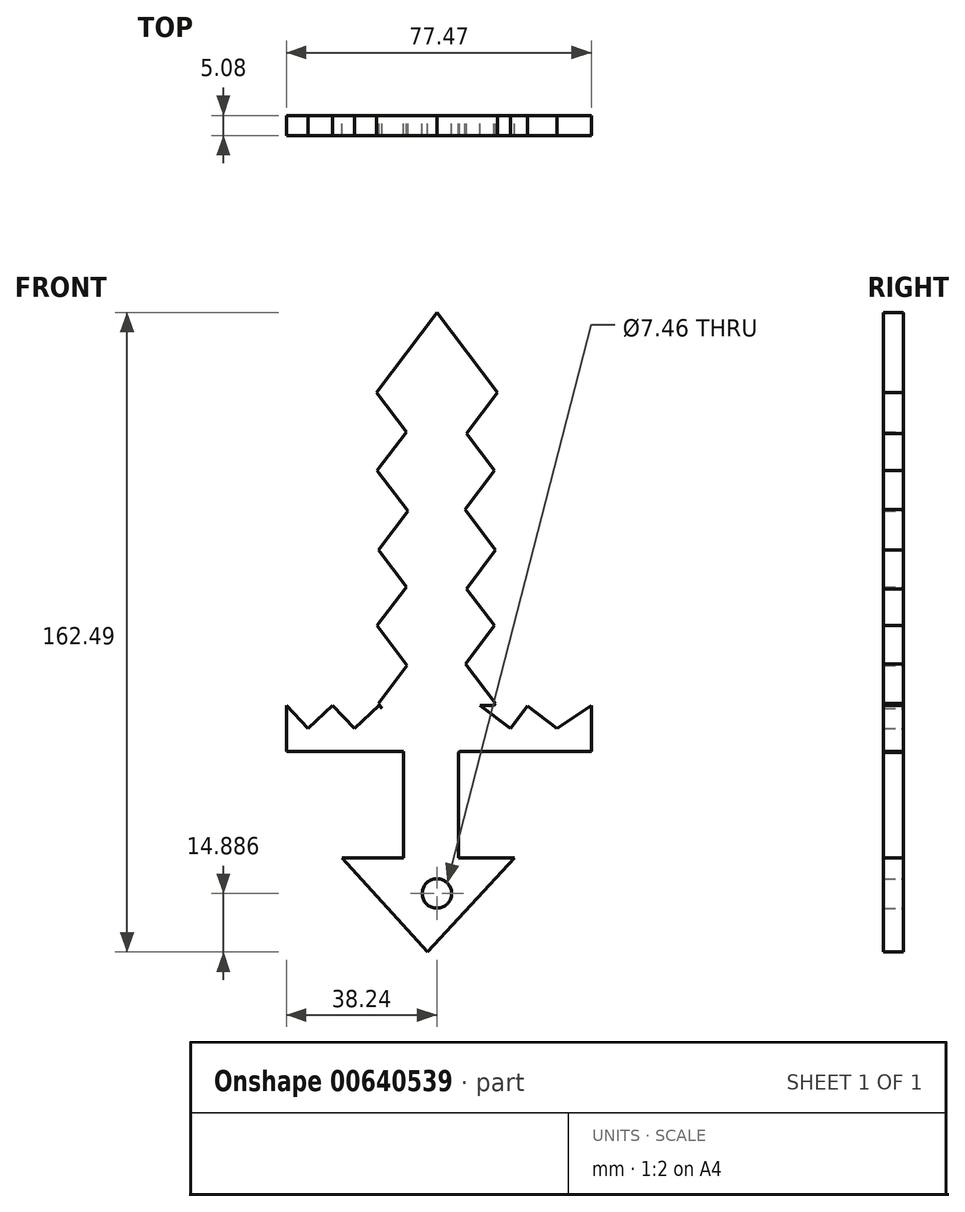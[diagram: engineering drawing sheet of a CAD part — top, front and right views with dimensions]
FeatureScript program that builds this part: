
annotation { "Feature Type Name" : "Feature", "Feature Type Description" : "" }
export const myFeature = defineFeature(function(context is Context, id is Id, definition is map)
    precondition{}
    {
        {
            var Q0;
            Q0=qCreatedBy(makeId("Front.planeOp"),FACE);
            var sketch = newSketch(context, id + "F0", { "sketchPlane" : qUnion([Q0])});
            skLineSegment(sketch, "E0", {"start": v(7.49, 9.92) * mm, "end": v(14.88, 19.71) * mm});
            skLineSegment(sketch, "E1", {"start": v(14.88, 19.71) * mm, "end": v(0, 39.43) * mm});
            skLineSegment(sketch, "E2", {"start": v(0, 39.43) * mm, "end": v(-14.88, 19.71) * mm});
            skLineSegment(sketch, "E3", {"start": v(-14.88, 19.71) * mm, "end": v(-7.79, 10.32) * mm});
            skLineSegment(sketch, "E4", {"start": v(7.26, -9.18) * mm, "end": v(14.58, 0.53) * mm});
            skLineSegment(sketch, "E5", {"start": v(14.58, 0.53) * mm, "end": v(-0.3, 20.24) * mm});
            skLineSegment(sketch, "E6", {"start": v(-0.3, 20.24) * mm, "end": v(-15.17, 0.53) * mm});
            skLineSegment(sketch, "E7", {"start": v(-15.17, 0.53) * mm, "end": v(-7.55, -9.57) * mm});
            skLineSegment(sketch, "E8", {"start": v(7.1, 30.03) * mm, "end": v(14.58, 39.95) * mm});
            skLineSegment(sketch, "E9", {"start": v(14.58, 39.95) * mm, "end": v(-0.3, 59.67) * mm});
            skLineSegment(sketch, "E10", {"start": v(-0.3, 59.67) * mm, "end": v(-15.17, 39.95) * mm});
            skLineSegment(sketch, "E11", {"start": v(-15.17, 39.95) * mm, "end": v(-7.39, 29.64) * mm});
            skLineSegment(sketch, "E12", {"start": v(5.48, -31.73) * mm, "end": v(5.69, -31.45) * mm});
            skLineSegment(sketch, "E13", {"start": v(14.88, -19.27) * mm, "end": v(0, 0.44) * mm});
            skLineSegment(sketch, "E14", {"start": v(0, 0.44) * mm, "end": v(-14.88, -19.27) * mm});
            skLineSegment(sketch, "E15", {"start": v(-14.88, -19.27) * mm, "end": v(-13.97, -20.47) * mm});
            skLineSegment(sketch, "E16", {"start": v(7.49, 49.35) * mm, "end": v(15.35, 59.76) * mm});
            skLineSegment(sketch, "E17", {"start": v(15.35, 59.76) * mm, "end": v(0, 80.1) * mm});
            skLineSegment(sketch, "E18", {"start": v(0, 80.1) * mm, "end": v(-15.35, 59.76) * mm});
            skLineSegment(sketch, "E19", {"start": v(-15.35, 59.76) * mm, "end": v(-7.79, 49.74) * mm});
            skLineSegment(sketch, "E20.bottom", {"start": v(-38.24, -19.7) * mm, "end": v(39.23, -19.7) * mm});
            skLineSegment(sketch, "E20.top", {"start": v(-38.24, -31.45) * mm, "end": v(39.23, -31.45) * mm});
            skLineSegment(sketch, "E20.left", {"start": v(-38.24, -19.7) * mm, "end": v(-38.24, -31.45) * mm});
            skLineSegment(sketch, "E20.right", {"start": v(39.23, -19.7) * mm, "end": v(39.23, -31.45) * mm});
            skLineSegment(sketch, "E21", {"start": v(-8.44, -31.45) * mm, "end": v(-8.44, -58.53) * mm});
            skLineSegment(sketch, "E22", {"start": v(5.48, -31.45) * mm, "end": v(5.48, -58.53) * mm});
            skLineSegment(sketch, "E23", {"start": v(-38.24, -19.7) * mm, "end": v(-32.68, -25.57) * mm});
            skPoint(sketch, "E23.endSnap0", {"position": v(-38.24, -25.57) * mm});
            skLineSegment(sketch, "E24", {"start": v(-32.68, -25.57) * mm, "end": v(-26.48, -19.7) * mm});
            skLineSegment(sketch, "E25", {"start": v(-26.48, -19.7) * mm, "end": v(-20.91, -25.57) * mm});
            skLineSegment(sketch, "E26", {"start": v(-20.91, -25.57) * mm, "end": v(-14.7, -19.7) * mm});
            skLineSegment(sketch, "E27", {"start": v(-14.7, -19.7) * mm, "end": v(-9.14, -25.57) * mm});
            skLineSegment(sketch, "E28", {"start": v(-9.14, -25.57) * mm, "end": v(-1.03, -19.91) * mm});
            skLineSegment(sketch, "E29", {"start": v(-1.03, -19.91) * mm, "end": v(6.47, -25.57) * mm});
            skLineSegment(sketch, "E30", {"start": v(6.47, -25.57) * mm, "end": v(10.9, -19.7) * mm});
            skLineSegment(sketch, "E31", {"start": v(10.9, -19.7) * mm, "end": v(18.69, -25.57) * mm});
            skLineSegment(sketch, "E32", {"start": v(18.69, -25.57) * mm, "end": v(22.96, -19.91) * mm});
            skLineSegment(sketch, "E33", {"start": v(22.96, -19.91) * mm, "end": v(30.46, -25.57) * mm});
            skLineSegment(sketch, "E34", {"start": v(30.46, -25.57) * mm, "end": v(39.23, -19.7) * mm});
            skPoint(sketch, "E35.visualSharp", {"position": v(5.48, -58.2) * mm});
            skPoint(sketch, "E36.visualSharp", {"position": v(-8.44, -58.2) * mm});
            skLineSegment(sketch, "E37.trimOffspring", {"start": v(14.56, -19.7) * mm, "end": v(14.88, -19.27) * mm});
            skPoint(sketch, "E38.trimOffspring.end.orphan", {"position": v(0, -38.99) * mm});
            skPoint(sketch, "E39.start.orphan", {"position": v(-13.97, -19.7) * mm});
            skLineSegment(sketch, "E40", {"start": v(-2.36, -82.4) * mm, "end": v(-24.17, -58.53) * mm});
            skLineSegment(sketch, "E41", {"start": v(-2.36, -82.4) * mm, "end": v(19.71, -58.53) * mm});
            skLineSegment(sketch, "E42", {"start": v(19.71, -58.53) * mm, "end": v(-24.17, -58.53) * mm});
            skCircle(sketch, "E43", {"center": v(0, -67.5) * mm, "radius": 3.73 * mm});
            skSolve(sketch);
        }
        {
            var Q0;
            {var subQ0=sQuery(id+"F0.wireOp",EDGE,"E16");Q0=makeQuery(id+"F0.imprint","IMPRINT",FACE,{"disambiguationData":[TD([[makeQuery(id+"F0.imprint","IMPRINT",EDGE,{"derivedFrom":subQ0}),1.0]])]});}
            var Q1;
            {var subQ5=sQuery(id+"F0.wireOp",EDGE,"E0");Q1=makeQuery(id+"F0.imprint","IMPRINT",FACE,{"disambiguationData":[TD([[makeQuery(id+"F0.imprint","IMPRINT",EDGE,{"derivedFrom":subQ5}),1.0]])]});}
            var Q2;
            {var subQ0=sQuery(id+"F0.wireOp",EDGE,"3IqZWeEq-TBCR-c4K0-hORi-1pJiHX5qmK4j");Q2=makeQuery(id+"F0.imprint","IMPRINT",FACE,{"disambiguationData":[TD([[makeQuery(id+"F0.imprint","IMPRINT",EDGE,{"derivedFrom":subQ0}),1.0]])]});}
            var Q3;
            {var subQ5=sQuery(id+"F0.wireOp",EDGE,"E4");Q3=makeQuery(id+"F0.imprint","IMPRINT",FACE,{"disambiguationData":[TD([[makeQuery(id+"F0.imprint","IMPRINT",EDGE,{"derivedFrom":subQ5}),1.0]])]});}
            var Q4;
            {var subQ1=sQuery(id+"F0.wireOp",EDGE,"E8");Q4=makeQuery(id+"F0.imprint","IMPRINT",FACE,{"disambiguationData":[TD([[makeQuery(id+"F0.imprint","IMPRINT",EDGE,{"derivedFrom":subQ1}),1.0]])]});}
            var Q5;
            {var subQ2=sQuery(id+"F0.wireOp",EDGE,"E13");var subQ5=sQuery(id+"F0.wireOp",EDGE,"E12");var subQ6=makeQuery(id+"F0.imprint","INTERSECT",VERTEX,{"derivedFrom":[subQ5,subQ2]});Q5=makeQuery(id+"F0.imprint","IMPRINT",FACE,{"disambiguationData":[TD([[makeQuery(id+"F0.imprint","IMPRINT",EDGE,{"disambiguationData":[TD([[subQ6,1.0]])],"derivedFrom":subQ5}),1.0]])]});}
            var Q6;
            {var subQ1=sQuery(id+"F0.wireOp",EDGE,"E12");var subQ3=sQuery(id+"F0.wireOp",EDGE,"hIctDjYF-F5GC-o0Hi-SDRA-Uy10DUFzBYAj.bottom");var subQ4=makeQuery(id+"F0.imprint","INTERSECT",VERTEX,{"derivedFrom":[subQ1,subQ3]});Q6=makeQuery(id+"F0.imprint","IMPRINT",FACE,{"disambiguationData":[TD([[makeQuery(id+"F0.imprint","IMPRINT",EDGE,{"disambiguationData":[TD([[subQ4,1.0]])],"derivedFrom":subQ3}),-1.0]])]});}
            var Q7;
            {var subQ1=sQuery(id+"F0.wireOp",EDGE,"hIctDjYF-F5GC-o0Hi-SDRA-Uy10DUFzBYAj.left");Q7=makeQuery(id+"F0.imprint","IMPRINT",FACE,{"disambiguationData":[TD([[makeQuery(id+"F0.imprint","IMPRINT",EDGE,{"derivedFrom":subQ1}),1.0]])]});}
            var Q8;
            {var subQ1=sQuery(id+"F0.wireOp",EDGE,"E20.left");Q8=makeQuery(id+"F0.imprint","IMPRINT",FACE,{"disambiguationData":[TD([[makeQuery(id+"F0.imprint","IMPRINT",EDGE,{"derivedFrom":subQ1}),1.0]])]});}
            var Q9;
            {var subQ8=sQuery(id+"F0.wireOp",EDGE,"E13");var subQ11=makeQuery(id+"F0.imprint","INTERSECT",VERTEX,{"derivedFrom":[sQuery(id+"F0.wireOp",EDGE,"E4"),subQ8]});Q9=makeQuery(id+"F0.imprint","IMPRINT",FACE,{"disambiguationData":[TD([[makeQuery(id+"F0.imprint","IMPRINT",EDGE,{"disambiguationData":[TD([[subQ11,1.0]])],"derivedFrom":subQ8}),1.0]])]});}
            var Q10;
            {var subQ5=sQuery(id+"F0.wireOp",EDGE,"E21");Q10=makeQuery(id+"F0.imprint","IMPRINT",FACE,{"disambiguationData":[TD([[makeQuery(id+"F0.imprint","IMPRINT",EDGE,{"derivedFrom":subQ5}),1.0]])]});}
            var Q11;
            {var subQ0=sQuery(id+"F0.wireOp",EDGE,"E28");Q11=makeQuery(id+"F0.imprint","IMPRINT",FACE,{"disambiguationData":[TD([[makeQuery(id+"F0.imprint","IMPRINT",EDGE,{"derivedFrom":subQ0}),1.0]])]});}
            var Q12;
            {var subQ4=sQuery(id+"F0.wireOp",EDGE,"E40");Q12=makeQuery(id+"F0.imprint","IMPRINT",FACE,{"disambiguationData":[TD([[makeQuery(id+"F0.imprint","IMPRINT",EDGE,{"derivedFrom":subQ4}),-1.0]])]});}
            extrude(context, id + "F1", {"entities" : qUnion([Q0, Q1, Q2, Q3, Q4, Q5, Q6, Q7, Q8, Q9, Q10, Q11, Q12]), "depth" : 5.08 * mm, "offsetDistance" : 25.4 * mm});
        }
    });
